# Revit family: Lighting_Fixtures-Wall-Astro-Tango 2700K v2
name_source: partatom
category: Lighting Fixtures
revit_build: Autodesk Revit 2018 (Build: 20170223_1515(x64)
units: mm (PartAtom-declared; Revit-internal decimal feet)

## family parameters
Cut with Voids When Loaded = No
Host = Face
Light Source = Yes
OmniClass Number = 23.80.70.00
OmniClass Title = Lighting
Part Type = Normal
Room Calculation Point = No
Round Connector Dimension = Use Diameter
Shared = No

## types (1)
- Tango 2700K
    Apparent Load = 4 VA
    Assembly Code = D5020200
    Color Filter = 16777215
    Description = Wall light
    Dimmable = Yes
    Dimming Lamp Color Temperature Shift = <None>
    Dimming Method = Driver dependent
    Driver Included = No
    Driver Required = Yes
    Efficacy (ln/W) = 11.23
    Electrical Class = 3
    Lamp = LED (Integral)
    Length of Cable Supplied (mm) = 1000 mm  [stored 3.28084 ft]
    Light Source Fixed = Yes
    Location Rating = IP65
    Main Finish = Various
    Main Material = Various
    Manufacturer = Astro Lighting Ltd, CM20 2DP
    Model = 0825 Tango White
    Photometric Web File = GNC-19554  7522 - Tango LED marker light white - 2700K ies.ies
    Power (Watts) = 2.6W
    Product Documentation = http://www.astrolighting.co.uk
    Product Location = Bathroom
    Tilt Angle = 0.00°
    Type Comments = Wall box provided with fitting. Driver not included.
    URL = www.astrolighting.co.uk

note: [stored X ft] marks values corroborated as IEEE doubles in the binary element streams (Revit-internal decimal feet)

## geometry (parser evidence)
native form markers: Sweep x5
no freeform markers — native parametric forms only
